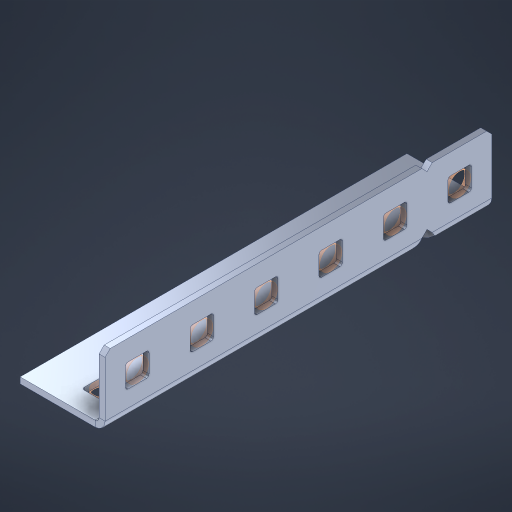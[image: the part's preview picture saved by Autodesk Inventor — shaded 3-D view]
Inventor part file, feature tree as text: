
AUTODESK INVENTOR PART (.ipt)
format: ipt  version: 2023 (Build 270158000, 158)  size: 478,720 bytes
history: native  units: in
note: dims shown in document units (in); Inventor stores cm internally (conversion verified against a paired STEP export)
features: other x17, extrude x11, sheet_metal_op x10, sketch x8, mirror x1, pattern_linear x1, chamfer x1
ambient origin geometry x8: Origin, YZ Plane, XZ Plane, XY Plane, X Axis, Y Axis, Z Axis, Center Point
bodies: Solid1 (feature_tree), Body (feature_tree)
feature tree (49):
  other  "Flange Pattern Plane"
  sheet_metal_op  "Flange Pattern"
  sheet_metal_op  "Body Pattern"
  other  "Arc Length"
  mirror  "Notch Mirror"
  pattern_linear  "Notch Pattern"  Spacing1=0.1875in  [1 undecoded]
  chamfer  "End Chamfer"
  extrude  "Half Cut"  Depth=0.0469in
  sketch  "Sketch1"  dims[d0=2.5in]
  other  "Plate1"
  sketch  "Sketch2"  dims[d1=3.0in]
  other  "Plate2"
  sheet_metal_op  "Bend1"
  sheet_metal_op  "Corner1"
  sketch  "Sketch3"  dims[d2=0.0469in]
  other  "Flange Pattern Sketch"
  sketch  "Sketch7"  dims[d3=0.0469in]
  other  "Srf1"
  other  "Srf2"
  sketch  "Sketch8"  dims[d4=0.0234in]
  sketch  "Sketch9"  dims[d5=0.0938in]
  other  "Srf91"
  sheet_metal_op  "Body Pattern Sketch"
  other  "Srf92"
  sketch  "Sketch13"  dims[d6=0.0469in]
  sketch  "Sketch14"  dims[d7=0.5in d8=90.0deg d9=0.0312in d10=0.1875in d11=0.0469in d12=0.0469in d16=0.182in d17=0.02in d18=0.0469in d19=0.0in d20=0.25in d21=0.25in d46=0.172in d47=1.0in d48=0.0in d49=0.182in d50=0.02in d51=0.25in d52=0.25in d53=0.0469in d54=0.0in d55=0.172in d56=1.0in d57=0.0in d60=2.3622in d62=0.5in d63=0.3937in d65=0.5in d85=0.1227in d86=0.1659in d88=0.04in d89=0.0469in d90=0.0in d91=0.04in d92=0.0491in d95=2.5in d96=0.04in d97=0.25in d98=45.0deg d101=0.0in d102=2.497in d131=0.5in d132=2.3622in d134=0.5in d139=0.5in]
  other  "Srf856"
  other  "Srf1310"
  other  "Srf1311"
  other  "Srf1312"
  other  "Srf1376"
  other  "Srf1377"
  other  "Srf1728"
  other  "Srf1755"
  sheet_metal_op  "Flange Stamp"
  sheet_metal_op  "Flange Circle"
  sheet_metal_op  "Body Stamp"
  sheet_metal_op  "Body Circle"
  sheet_metal_op  "Notch"
  extrude  "ExtrusionSrf2"  Depth=0.0469in
  extrude  "ExtrusionSrf92"  Depth=0.5in
  extrude  "ExtrusionSrf856"  Depth=0.02in
  extrude  "ExtrusionSrf1310"  Depth=0.0469in
  extrude  "ExtrusionSrf1311"  TaperAngle=0.0deg  [1 undecoded]
  extrude  "ExtrusionSrf1312"  Depth=0.5in
  extrude  "ExtrusionSrf1376"  Depth=0.5in
  extrude  "ExtrusionSrf1377"  Depth=0.5in
  extrude  "ExtrusionSrf1728"  Depth=0.5in TaperAngle=0.0deg
  extrude  "ExtrusionSrf1755"  Depth=0.5in
note: 2 required parameter values undecoded (feature->parameter linkage not recoverable at this tier; creation-order binding heuristic only, values carry confidence <= 0.55)
